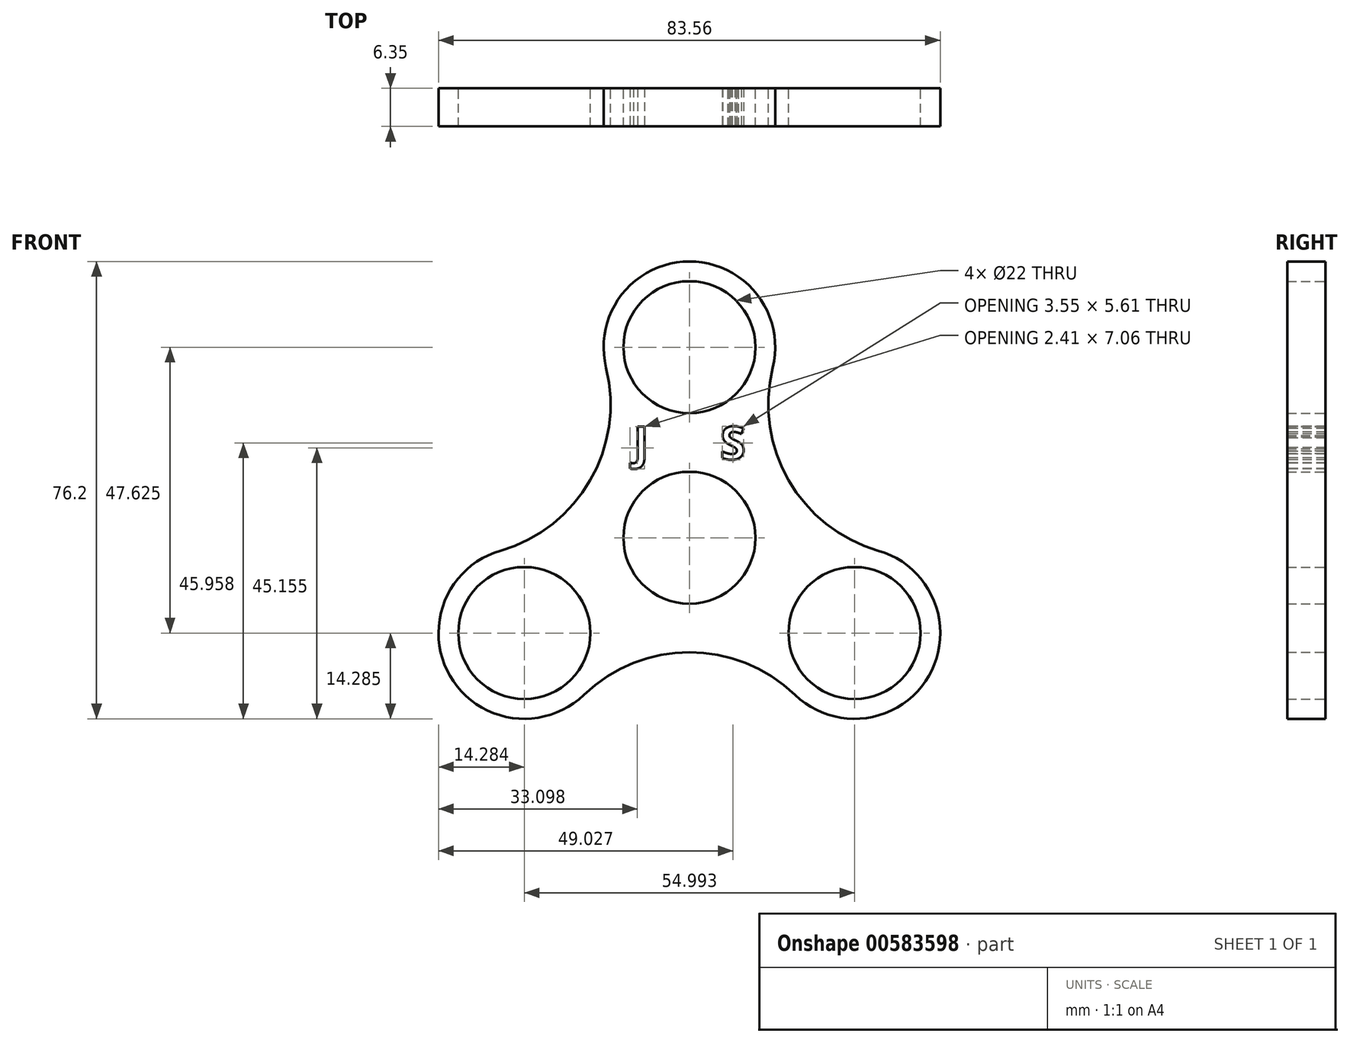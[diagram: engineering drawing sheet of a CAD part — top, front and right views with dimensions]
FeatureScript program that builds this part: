
annotation { "Feature Type Name" : "Feature", "Feature Type Description" : "" }
export const myFeature = defineFeature(function(context is Context, id is Id, definition is map)
    precondition{}
    {
        {
            var Q0;
            Q0=qCreatedBy(makeId("Front.planeOp"),FACE);
            var sketch = newSketch(context, id + "F0", { "sketchPlane" : qUnion([Q0])});
            skCircle(sketch, "E0", {"center": v(0, 0) * mm, "radius": 14.29 * mm});
            skCircle(sketch, "E1", {"center": v(0, 0) * mm, "radius": 11 * mm});
            skCircle(sketch, "E2", {"center": v(0, 31.75) * mm, "radius": 11 * mm});
            skCircle(sketch, "E3", {"center": v(0, 31.75) * mm, "radius": 14.29 * mm});
            skCircle(sketch, "E4.1.0", {"center": v(-27.5, -15.87) * mm, "radius": 14.29 * mm});
            skCircle(sketch, "E4.2.0", {"center": v(27.5, -15.88) * mm, "radius": 14.29 * mm});
            skCircle(sketch, "E5.1.0", {"center": v(-27.5, -15.87) * mm, "radius": 11 * mm});
            skCircle(sketch, "E5.2.0", {"center": v(27.5, -15.88) * mm, "radius": 11 * mm});
            skSolve(sketch);
        }
        {
            var Q0;
            Q0=qCreatedBy(makeId("Front.planeOp"),FACE);
            var sketch = newSketch(context, id + "F1", { "sketchPlane" : qUnion([Q0])});
            skArc(sketch, "E6", {"start": v(13.87, 28.33) * mm, "mid": v(16.54, 9.55) * mm, "end": v(31.47, -2.15) * mm});
            skArc(sketch, "E7", {"start": v(17.6, -26.18) * mm, "mid": v(0, -19.1) * mm, "end": v(-17.6, -26.18) * mm});
            skCircle(sketch, "E8", {"center": v(0, 31.75) * mm, "radius": 14.29 * mm});
            skCircle(sketch, "E9", {"center": v(0, 31.75) * mm, "radius": 11 * mm});
            skArc(sketch, "E10", {"start": v(-31.47, -2.15) * mm, "mid": v(-16.54, 9.55) * mm, "end": v(-13.87, 28.33) * mm});
            skCircle(sketch, "E11.0", {"center": v(-27.5, -15.87) * mm, "radius": 14.29 * mm});
            skCircle(sketch, "E12.0", {"center": v(0, 0) * mm, "radius": 14.29 * mm});
            skCircle(sketch, "E13.0", {"center": v(27.5, -15.88) * mm, "radius": 14.29 * mm});
            skCircle(sketch, "E14.0", {"center": v(-27.5, -15.87) * mm, "radius": 11 * mm});
            skCircle(sketch, "E15.0.0", {"center": v(27.5, -15.88) * mm, "radius": 11 * mm});
            skCircle(sketch, "E16.0", {"center": v(0, 0) * mm, "radius": 11 * mm});
            skSolve(sketch);
        }
        {
            var Q0;
            Q0 = qSketchRegion(id + "F1", true);
            extrude(context, id + "F2", {"entities" : qUnion([Q0]), "depth" : 6.35 * mm, "offsetDistance" : 25.4 * mm});
        }
        {
            var Q0;
            Q0=makeQuery(id+"F2.opExtrude","CAP_FACE",FACE,{"disambiguationData":[OSD([sQuery(id+"F1.wireOp",EDGE,"E6"),sQuery(id+"F1.wireOp",EDGE,"E7"),sQuery(id+"F1.wireOp",EDGE,"E8"),sQuery(id+"F1.wireOp",EDGE,"E9"),sQuery(id+"F1.wireOp",EDGE,"E10"),sQuery(id+"F1.wireOp",EDGE,"E11.0"),sQuery(id+"F1.wireOp",EDGE,"E12.0"),sQuery(id+"F1.wireOp",EDGE,"E13.0"),sQuery(id+"F1.wireOp",EDGE,"E14.0"),sQuery(id+"F1.wireOp",EDGE,"E15.0.0")])],"isStart":false});
            var sketch = newSketch(context, id + "F3", { "sketchPlane" : qUnion([Q0])});
            skText(sketch, "E17", { "text": "J      S", "fontName": "OpenSans-Bold.ttf"});
            const initialGuessF3  = {"E17": [-0.00932, 0.01307, 1, 0, 0.0055]};
            skSetInitialGuess(sketch, initialGuessF3);
            skSolve(sketch);
        }
        {
            var Q0;
            Q0 = qSketchRegion(id + "F3", true);
            extrude(context, id + "F4", {"entities" : qUnion([Q0]), "operationType" : NewBodyOperationType.REMOVE, "oppositeDirection" : true, "depth" : 25.4 * mm, "offsetDistance" : 25.4 * mm});
        }
        {
            var Q0;
            Q0=makeQuery(id+"F0.imprint","IMPRINT",FACE,{"disambiguationData":[TD([[makeQuery(id+"F0.imprint","IMPRINT",EDGE,{"derivedFrom":sQuery(id+"F0.wireOp",EDGE,"E0")}),1.0]])]});
            extrude(context, id + "F5", {"entities" : qUnion([Q0]), "operationType" : NewBodyOperationType.ADD, "depth" : 6.35 * mm, "offsetDistance" : 25.4 * mm});
        }
    });
